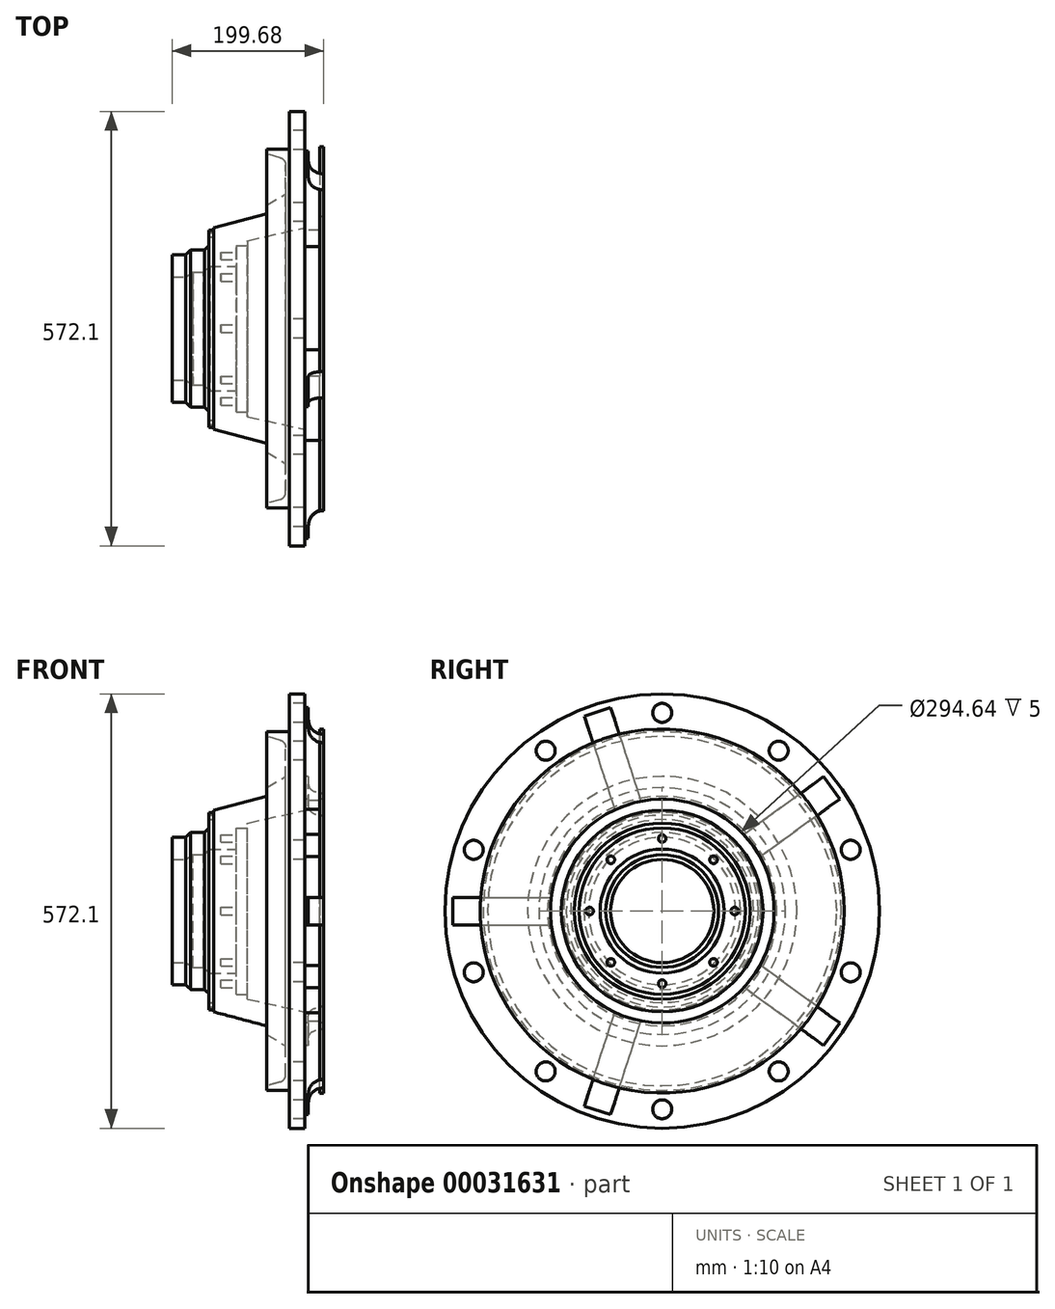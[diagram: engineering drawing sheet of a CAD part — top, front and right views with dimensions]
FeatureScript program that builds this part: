
annotation { "Feature Type Name" : "Feature", "Feature Type Description" : "" }
export const myFeature = defineFeature(function(context is Context, id is Id, definition is map)
    precondition{}
    {
        {
            var Q0;
            Q0=qCreatedBy(makeId("Front.planeOp"),FACE);
            var sketch = newSketch(context, id + "F0", { "sketchPlane" : qUnion([Q0])});
            skLineSegment(sketch, "E0", {"start": v(-16.31, 151.18) * mm, "end": v(-16.31, 189.2) * mm});
            skLineSegment(sketch, "E1", {"start": v(-23.64, 198.84) * mm, "end": v(-41.31, 203.73) * mm});
            skLineSegment(sketch, "E2", {"start": v(-41.31, 203.73) * mm, "end": v(-41.31, 209.73) * mm});
            skLineSegment(sketch, "E3", {"start": v(-41.31, 209.73) * mm, "end": v(-11.31, 209.73) * mm});
            skLineSegment(sketch, "E4", {"start": v(-11.31, 209.73) * mm, "end": v(-11.31, 259.73) * mm});
            skLineSegment(sketch, "E5", {"start": v(-11.31, 259.73) * mm, "end": v(8.69, 259.73) * mm});
            skLineSegment(sketch, "E6", {"start": v(8.69, 106.48) * mm, "end": v(-66.31, 89.52) * mm});
            skLineSegment(sketch, "E7", {"start": v(-66.31, 89.52) * mm, "end": v(-66.31, 83.17) * mm});
            skPoint(sketch, "E8.visualSharp", {"position": v(-16.31, 196.81) * mm});
            skArc(sketch, "E8.filletArc", {"start": v(-16.31, 189.2) * mm, "mid": v(-18.36, 195.26) * mm, "end": v(-23.64, 198.84) * mm});
            skLineSegment(sketch, "E9", {"start": v(-41.31, 124.8) * mm, "end": v(-41.31, 136.18) * mm});
            skLineSegment(sketch, "E10", {"start": v(-41.31, 136.18) * mm, "end": v(-16.31, 151.18) * mm});
            skLineSegment(sketch, "E11", {"start": v(-111.31, 106.4) * mm, "end": v(-41.31, 124.8) * mm});
            skLineSegment(sketch, "E12", {"start": v(-66.31, 83.17) * mm, "end": v(-81.31, 83.17) * mm});
            skLineSegment(sketch, "E13", {"start": v(-81.31, 83.17) * mm, "end": v(-81.31, 55.36) * mm});
            skLineSegment(sketch, "E14", {"start": v(-110.7, 106.4) * mm, "end": v(-111.31, 106.4) * mm});
            skLineSegment(sketch, "E15", {"start": v(-110.7, 106.4) * mm, "end": v(-110.7, 103.57) * mm});
            skLineSegment(sketch, "E16", {"start": v(-110.7, 103.57) * mm, "end": v(-117.24, 103.57) * mm});
            skLineSegment(sketch, "E17", {"start": v(-117.24, 103.57) * mm, "end": v(-117.24, 100.15) * mm});
            skLineSegment(sketch, "E18", {"start": v(-117.24, 100.15) * mm, "end": v(-110.7, 100.15) * mm});
            skLineSegment(sketch, "E19", {"start": v(-110.7, 100.15) * mm, "end": v(-110.7, 94.23) * mm});
            skLineSegment(sketch, "E20", {"start": v(-110.7, 94.23) * mm, "end": v(-117.24, 94.23) * mm});
            skLineSegment(sketch, "E21", {"start": v(-117.24, 94.23) * mm, "end": v(-117.24, 82.72) * mm});
            skLineSegment(sketch, "E22", {"start": v(-117.24, 82.72) * mm, "end": v(-123.31, 76.96) * mm});
            skLineSegment(sketch, "E23", {"start": v(-123.31, 76.96) * mm, "end": v(-141.31, 76.96) * mm});
            skLineSegment(sketch, "E24", {"start": v(-141.31, 76.96) * mm, "end": v(-148, 70.74) * mm});
            skLineSegment(sketch, "E25", {"start": v(-148, 70.74) * mm, "end": v(-166, 70.74) * mm});
            skLineSegment(sketch, "E26", {"start": v(-81.31, 55.36) * mm, "end": v(-116.31, 55.36) * mm});
            skLineSegment(sketch, "E27", {"start": v(-116.31, 55.36) * mm, "end": v(-124.55, 47.96) * mm});
            skLineSegment(sketch, "E28", {"start": v(-124.55, 47.96) * mm, "end": v(-138.27, 47.96) * mm});
            skLineSegment(sketch, "E29", {"start": v(-138.27, 47.96) * mm, "end": v(-147.69, 41.68) * mm});
            skLineSegment(sketch, "E30", {"start": v(-166, 70.74) * mm, "end": v(-166, -26.32) * mm});
            skLineSegment(sketch, "E31", {"start": v(8.69, 259.73) * mm, "end": v(8.69, -26.32) * mm});
            skLineSegment(sketch, "E32", {"start": v(8.69, -26.32) * mm, "end": v(-166, -26.32) * mm, "construction": true});
            skLineSegment(sketch, "E33", {"start": v(-147.69, 41.68) * mm, "end": v(-166, 41.68) * mm});
            skSolve(sketch);
        }
        {
            var Q0;
            Q0=makeQuery(id+"F0.imprint","IMPRINT",FACE,{"disambiguationData":[TD([[makeQuery(id+"F0.imprint","IMPRINT",EDGE,{"derivedFrom":sQuery(id+"F0.wireOp",EDGE,"E0")}),-1.0]])]});
            var Q1;
            Q1=sQuery(id+"F0.wireOp",EDGE,"E32");
            revolve(context, id + "F1", {"entities" : qUnion([Q0]), "axis" : qUnion([Q1]), "revolveType" : RevolveType.FULL});
        }
        {
            var Q0;
            Q0=makeQuery(id+"F1.opRevolve","SWEPT_FACE",FACE,{"disambiguationData":[OSD([sQuery(id+"F0.wireOp",EDGE,"E4")])]});
            var sketch = newSketch(context, id + "F2", { "sketchPlane" : qUnion([Q0])});
            skCircle(sketch, "E34", {"center": v(0, 234.73) * mm, "radius": 12.5 * mm});
            skPoint(sketch, "E35", {"position": v(0, -26.32) * mm});
            skCircle(sketch, "E36.1.0", {"center": v(-153.44, 184.88) * mm, "radius": 12.5 * mm});
            skCircle(sketch, "E36.2.0", {"center": v(-248.27, 54.35) * mm, "radius": 12.5 * mm});
            skCircle(sketch, "E36.3.0", {"center": v(-248.27, -106.99) * mm, "radius": 12.5 * mm});
            skCircle(sketch, "E36.4.0", {"center": v(-153.44, -237.51) * mm, "radius": 12.5 * mm});
            skCircle(sketch, "E36.5.0", {"center": v(0, -287.37) * mm, "radius": 12.5 * mm});
            skCircle(sketch, "E36.6.0", {"center": v(153.44, -237.51) * mm, "radius": 12.5 * mm});
            skCircle(sketch, "E36.7.0", {"center": v(248.27, -106.99) * mm, "radius": 12.5 * mm});
            skCircle(sketch, "E36.8.0", {"center": v(248.27, 54.35) * mm, "radius": 12.5 * mm});
            skCircle(sketch, "E36.9.0", {"center": v(153.44, 184.88) * mm, "radius": 12.5 * mm});
            skSolve(sketch);
        }
        {
            var Q0;
            Q0 = qSketchRegion(id + "F2", true);
            extrude(context, id + "F3", {"entities" : qUnion([Q0]), "operationType" : NewBodyOperationType.REMOVE, "oppositeDirection" : true, "depth" : 20 * mm});
        }
        {
            var Q0;
            Q0=makeQuery(id+"F1.opRevolve","SWEPT_FACE",FACE,{"disambiguationData":[OSD([sQuery(id+"F0.wireOp",EDGE,"E13")])]});
            var sketch = newSketch(context, id + "F4", { "sketchPlane" : qUnion([Q0])});
            skCircle(sketch, "E37", {"center": v(0, 69.27) * mm, "radius": 5 * mm});
            skPoint(sketch, "E38", {"position": v(0, -26.32) * mm});
            skCircle(sketch, "E39.1.0", {"center": v(-67.59, 41.27) * mm, "radius": 5 * mm});
            skCircle(sketch, "E39.2.0", {"center": v(-95.59, -26.32) * mm, "radius": 5 * mm});
            skCircle(sketch, "E39.3.0", {"center": v(-67.59, -93.9) * mm, "radius": 5 * mm});
            skCircle(sketch, "E39.4.0", {"center": v(0, -121.9) * mm, "radius": 5 * mm});
            skCircle(sketch, "E39.5.0", {"center": v(67.59, -93.9) * mm, "radius": 5 * mm});
            skCircle(sketch, "E39.6.0", {"center": v(95.59, -26.32) * mm, "radius": 5 * mm});
            skCircle(sketch, "E39.7.0", {"center": v(67.59, 41.27) * mm, "radius": 5 * mm});
            skSolve(sketch);
        }
        {
            var Q0;
            Q0 = qSketchRegion(id + "F4", true);
            extrude(context, id + "F5", {"entities" : qUnion([Q0]), "operationType" : NewBodyOperationType.REMOVE, "oppositeDirection" : true, "depth" : 20 * mm});
        }
        {
            var Q0;
            Q0=makeQuery(id+"F1.opRevolve","SWEPT_FACE",FACE,{"disambiguationData":[OSD([sQuery(id+"F0.wireOp",EDGE,"E31")])]});
            var sketch = newSketch(context, id + "F6", { "sketchPlane" : qUnion([Q0])});
            skLineSegment(sketch, "E40.bottom", {"start": v(-276.03, -44.49) * mm, "end": v(-147, -44.49) * mm});
            skLineSegment(sketch, "E40.top", {"start": v(-276.03, -8.15) * mm, "end": v(-147, -8.15) * mm});
            skLineSegment(sketch, "E40.left", {"start": v(-276.03, -44.49) * mm, "end": v(-276.03, -8.15) * mm});
            skLineSegment(sketch, "E40.right", {"start": v(-147, -44.49) * mm, "end": v(-147, -8.15) * mm});
            skLineSegment(sketch, "E41.1.0", {"start": v(-68.02, -294.45) * mm, "end": v(-102.58, -283.22) * mm});
            skLineSegment(sketch, "E41.1.1", {"start": v(-68.02, -294.45) * mm, "end": v(-28.15, -171.74) * mm});
            skLineSegment(sketch, "E41.1.2", {"start": v(-102.58, -283.22) * mm, "end": v(-62.7, -160.51) * mm});
            skLineSegment(sketch, "E41.1.3", {"start": v(-28.15, -171.74) * mm, "end": v(-62.7, -160.51) * mm});
            skLineSegment(sketch, "E41.2.0", {"start": v(234, -173.86) * mm, "end": v(212.63, -203.26) * mm});
            skLineSegment(sketch, "E41.2.1", {"start": v(234, -173.86) * mm, "end": v(129.6, -98.02) * mm});
            skLineSegment(sketch, "E41.2.2", {"start": v(212.63, -203.26) * mm, "end": v(108.25, -127.42) * mm});
            skLineSegment(sketch, "E41.2.3", {"start": v(129.6, -98.02) * mm, "end": v(108.25, -127.42) * mm});
            skLineSegment(sketch, "E41.3.0", {"start": v(212.63, 150.63) * mm, "end": v(234, 121.23) * mm});
            skLineSegment(sketch, "E41.3.1", {"start": v(212.63, 150.63) * mm, "end": v(108.25, 74.79) * mm});
            skLineSegment(sketch, "E41.3.2", {"start": v(234, 121.23) * mm, "end": v(129.6, 45.4) * mm});
            skLineSegment(sketch, "E41.3.3", {"start": v(108.25, 74.79) * mm, "end": v(129.6, 45.4) * mm});
            skLineSegment(sketch, "E41.4.0", {"start": v(-102.58, 230.59) * mm, "end": v(-68.02, 241.82) * mm});
            skLineSegment(sketch, "E41.4.1", {"start": v(-102.58, 230.59) * mm, "end": v(-62.7, 107.88) * mm});
            skLineSegment(sketch, "E41.4.2", {"start": v(-68.02, 241.82) * mm, "end": v(-28.15, 119.1) * mm});
            skLineSegment(sketch, "E41.4.3", {"start": v(-62.7, 107.88) * mm, "end": v(-28.15, 119.1) * mm});
            skPoint(sketch, "E41.center", {"position": v(0, -26.32) * mm});
            skSolve(sketch);
        }
        {
            var Q0;
            Q0 = qSketchRegion(id + "F6", true);
            extrude(context, id + "F7", {"entities" : qUnion([Q0]), "operationType" : NewBodyOperationType.ADD, "depth" : 20 * mm});
        }
        {
            var Q0;
            Q0=makeQuery(id+"F7.opExtrude","CAP_FACE",FACE,{"disambiguationData":[OSD([sQuery(id+"F6.wireOp",EDGE,"E40.bottom"),sQuery(id+"F6.wireOp",EDGE,"E40.top"),sQuery(id+"F6.wireOp",EDGE,"E40.left"),sQuery(id+"F6.wireOp",EDGE,"E40.right")])],"isStart":false});
            var sketch = newSketch(context, id + "F8", { "sketchPlane" : qUnion([Q0])});
            skCircle(sketch, "E42", {"center": v(0, -26.32) * mm, "radius": 239.7 * mm});
            skPoint(sketch, "E42.centerSnap0", {"position": v(-276.03, -26.32) * mm});
            skCircle(sketch, "E43", {"center": v(0, -26.32) * mm, "radius": 147.32 * mm});
            skSolve(sketch);
        }
        {
            var Q0;
            {var subQ1=makeQuery(id+"F7.opExtrude","CAP_EDGE",EDGE,{"disambiguationData":[OSD([sQuery(id+"F6.wireOp",EDGE,"E40.bottom")])],"isStart":false});var subQ3=sQuery(id+"F8.wireOp",EDGE,"E42");var subQ4=makeQuery(id+"F8.imprint","INTERSECT",VERTEX,{"derivedFrom":[subQ1,subQ3]});Q0=makeQuery(id+"F8.imprint","IMPRINT",FACE,{"disambiguationData":[TD([[makeQuery(id+"F8.imprint","IMPRINT",EDGE,{"disambiguationData":[TD([[subQ4,1.0]])],"derivedFrom":subQ3}),1.0]])]});}
            var Q1;
            {var subQ1=makeQuery(id+"F7.opExtrude","CAP_EDGE",EDGE,{"disambiguationData":[OSD([sQuery(id+"F6.wireOp",EDGE,"E40.bottom")])],"isStart":false});var subQ3=sQuery(id+"F8.wireOp",EDGE,"E42");var subQ4=makeQuery(id+"F8.imprint","INTERSECT",VERTEX,{"derivedFrom":[subQ1,subQ3]});Q1=makeQuery(id+"F8.imprint","IMPRINT",FACE,{"disambiguationData":[TD([[makeQuery(id+"F8.imprint","IMPRINT",EDGE,{"disambiguationData":[TD([[subQ4,-1.0]])],"derivedFrom":subQ3}),1.0]])]});}
            extrude(context, id + "F9", {"entities" : qUnion([Q0, Q1]), "operationType" : NewBodyOperationType.ADD, "depth" : 5 * mm});
        }
        {
            var Q0;
            {var subQ0=sQuery(id+"F6.wireOp",EDGE,"E41.1.2");var subQ2=sQuery(id+"F6.wireOp",EDGE,"E41.1.1");var subQ3=sQuery(id+"F6.wireOp",EDGE,"E41.1.0");Q0=makeQuery(id+"F9.boolean.opBoolean","SPLIT",FACE,{"disambiguationData":[TD([makeQuery(id+"F7.opExtrude","SWEPT_FACE",FACE,{"disambiguationData":[OSD([subQ3])]})])],"derivedFrom":makeQuery(id+"F7.opExtrude","CAP_FACE",FACE,{"disambiguationData":[OSD([subQ3,subQ2,subQ0,sQuery(id+"F6.wireOp",EDGE,"E41.1.3")])],"isStart":false})});}
            var Q1;
            {var subQ1=sQuery(id+"F6.wireOp",EDGE,"E40.left");var subQ2=sQuery(id+"F6.wireOp",EDGE,"E40.top");var subQ3=sQuery(id+"F6.wireOp",EDGE,"E40.bottom");Q1=makeQuery(id+"F9.boolean.opBoolean","SPLIT",FACE,{"disambiguationData":[TD([makeQuery(id+"F7.opExtrude","SWEPT_FACE",FACE,{"disambiguationData":[OSD([subQ3])]})])],"derivedFrom":makeQuery(id+"F7.opExtrude","CAP_FACE",FACE,{"disambiguationData":[OSD([subQ3,subQ2,subQ1,sQuery(id+"F6.wireOp",EDGE,"E40.right")])],"isStart":false})});}
            var Q2;
            {var subQ1=sQuery(id+"F6.wireOp",EDGE,"E41.2.2");var subQ2=sQuery(id+"F6.wireOp",EDGE,"E41.2.1");var subQ3=sQuery(id+"F6.wireOp",EDGE,"E41.2.0");Q2=makeQuery(id+"F9.boolean.opBoolean","SPLIT",FACE,{"disambiguationData":[TD([makeQuery(id+"F7.opExtrude","SWEPT_FACE",FACE,{"disambiguationData":[OSD([subQ3])]})])],"derivedFrom":makeQuery(id+"F7.opExtrude","CAP_FACE",FACE,{"disambiguationData":[OSD([subQ3,subQ2,subQ1,sQuery(id+"F6.wireOp",EDGE,"E41.2.3")])],"isStart":false})});}
            var Q3;
            {var subQ0=sQuery(id+"F6.wireOp",EDGE,"E41.4.2");var subQ2=sQuery(id+"F6.wireOp",EDGE,"E41.4.1");var subQ3=sQuery(id+"F6.wireOp",EDGE,"E41.4.0");Q3=makeQuery(id+"F9.boolean.opBoolean","SPLIT",FACE,{"disambiguationData":[TD([makeQuery(id+"F7.opExtrude","SWEPT_FACE",FACE,{"disambiguationData":[OSD([subQ3])]})])],"derivedFrom":makeQuery(id+"F7.opExtrude","CAP_FACE",FACE,{"disambiguationData":[OSD([subQ3,subQ2,subQ0,sQuery(id+"F6.wireOp",EDGE,"E41.4.3")])],"isStart":false})});}
            var Q4;
            {var subQ1=sQuery(id+"F6.wireOp",EDGE,"E41.3.2");var subQ2=sQuery(id+"F6.wireOp",EDGE,"E41.3.1");var subQ3=sQuery(id+"F6.wireOp",EDGE,"E41.3.0");Q4=makeQuery(id+"F9.boolean.opBoolean","SPLIT",FACE,{"disambiguationData":[TD([makeQuery(id+"F7.opExtrude","SWEPT_FACE",FACE,{"disambiguationData":[OSD([subQ3])]})])],"derivedFrom":makeQuery(id+"F7.opExtrude","CAP_FACE",FACE,{"disambiguationData":[OSD([subQ3,subQ2,subQ1,sQuery(id+"F6.wireOp",EDGE,"E41.3.3")])],"isStart":false})});}
            extrude(context, id + "F10", {"entities" : qUnion([Q0, Q1, Q2, Q3, Q4]), "operationType" : NewBodyOperationType.REMOVE, "oppositeDirection" : true, "depth" : 15 * mm});
        }
        {
            var Q0;
            {var subQ0=sQuery(id+"F8.wireOp",EDGE,"E42");Q0=makeQuery(id+"F10.boolean.opBoolean","COPY",EDGE,{"derivedFrom":makeQuery(id+"F10.opExtrude","CAP_EDGE",EDGE,{"disambiguationData":[OSD([subQ0]),TDD([makeQuery(id+"F9.boolean.opBoolean","SPLIT",EDGE,{"disambiguationData":[topologyDisambiguationEdgeConnected([makeQuery(id+"F7.opExtrude","CAP_FACE",FACE,{"disambiguationData":[OSD([sQuery(id+"F6.wireOp",EDGE,"E41.2.0"),sQuery(id+"F6.wireOp",EDGE,"E41.2.1"),sQuery(id+"F6.wireOp",EDGE,"E41.2.2"),sQuery(id+"F6.wireOp",EDGE,"E41.2.3")])],"isStart":false}),makeQuery(id+"F9.opExtrude","SWEPT_FACE",FACE,{"disambiguationData":[OSD([subQ0])]})])],"derivedFrom":makeQuery(id+"F9.opExtrude","CAP_EDGE",EDGE,{"disambiguationData":[OSD([subQ0])],"isStart":true})})])],"isStart":false})});}
            var Q1;
            {var subQ0=sQuery(id+"F8.wireOp",EDGE,"E42");Q1=makeQuery(id+"F10.boolean.opBoolean","COPY",EDGE,{"derivedFrom":makeQuery(id+"F10.opExtrude","CAP_EDGE",EDGE,{"disambiguationData":[OSD([subQ0]),TDD([makeQuery(id+"F9.boolean.opBoolean","SPLIT",EDGE,{"disambiguationData":[topologyDisambiguationEdgeConnected([makeQuery(id+"F7.opExtrude","CAP_FACE",FACE,{"disambiguationData":[OSD([sQuery(id+"F6.wireOp",EDGE,"E41.3.0"),sQuery(id+"F6.wireOp",EDGE,"E41.3.1"),sQuery(id+"F6.wireOp",EDGE,"E41.3.2"),sQuery(id+"F6.wireOp",EDGE,"E41.3.3")])],"isStart":false}),makeQuery(id+"F9.opExtrude","SWEPT_FACE",FACE,{"disambiguationData":[OSD([subQ0])]})])],"derivedFrom":makeQuery(id+"F9.opExtrude","CAP_EDGE",EDGE,{"disambiguationData":[OSD([subQ0])],"isStart":true})})])],"isStart":false})});}
            var Q2;
            {var subQ0=sQuery(id+"F8.wireOp",EDGE,"E42");Q2=makeQuery(id+"F10.boolean.opBoolean","COPY",EDGE,{"derivedFrom":makeQuery(id+"F10.opExtrude","CAP_EDGE",EDGE,{"disambiguationData":[OSD([subQ0]),TDD([makeQuery(id+"F9.boolean.opBoolean","SPLIT",EDGE,{"disambiguationData":[topologyDisambiguationEdgeConnected([makeQuery(id+"F7.opExtrude","CAP_FACE",FACE,{"disambiguationData":[OSD([sQuery(id+"F6.wireOp",EDGE,"E41.4.0"),sQuery(id+"F6.wireOp",EDGE,"E41.4.1"),sQuery(id+"F6.wireOp",EDGE,"E41.4.2"),sQuery(id+"F6.wireOp",EDGE,"E41.4.3")])],"isStart":false}),makeQuery(id+"F9.opExtrude","SWEPT_FACE",FACE,{"disambiguationData":[OSD([subQ0])]})])],"derivedFrom":makeQuery(id+"F9.opExtrude","CAP_EDGE",EDGE,{"disambiguationData":[OSD([subQ0])],"isStart":true})})])],"isStart":false})});}
            var Q3;
            {var subQ0=sQuery(id+"F8.wireOp",EDGE,"E42");Q3=makeQuery(id+"F10.boolean.opBoolean","COPY",EDGE,{"derivedFrom":makeQuery(id+"F10.opExtrude","CAP_EDGE",EDGE,{"disambiguationData":[OSD([subQ0]),TDD([makeQuery(id+"F9.boolean.opBoolean","SPLIT",EDGE,{"disambiguationData":[topologyDisambiguationEdgeConnected([makeQuery(id+"F7.opExtrude","CAP_FACE",FACE,{"disambiguationData":[OSD([sQuery(id+"F6.wireOp",EDGE,"E40.bottom"),sQuery(id+"F6.wireOp",EDGE,"E40.top"),sQuery(id+"F6.wireOp",EDGE,"E40.left"),sQuery(id+"F6.wireOp",EDGE,"E40.right")])],"isStart":false}),makeQuery(id+"F9.opExtrude","SWEPT_FACE",FACE,{"disambiguationData":[OSD([subQ0])]})])],"derivedFrom":makeQuery(id+"F9.opExtrude","CAP_EDGE",EDGE,{"disambiguationData":[OSD([subQ0])],"isStart":true})})])],"isStart":false})});}
            var Q4;
            {var subQ0=sQuery(id+"F8.wireOp",EDGE,"E42");Q4=makeQuery(id+"F10.boolean.opBoolean","COPY",EDGE,{"derivedFrom":makeQuery(id+"F10.opExtrude","CAP_EDGE",EDGE,{"disambiguationData":[OSD([subQ0]),TDD([makeQuery(id+"F9.boolean.opBoolean","SPLIT",EDGE,{"disambiguationData":[topologyDisambiguationEdgeConnected([makeQuery(id+"F7.opExtrude","CAP_FACE",FACE,{"disambiguationData":[OSD([sQuery(id+"F6.wireOp",EDGE,"E41.1.0"),sQuery(id+"F6.wireOp",EDGE,"E41.1.1"),sQuery(id+"F6.wireOp",EDGE,"E41.1.2"),sQuery(id+"F6.wireOp",EDGE,"E41.1.3")])],"isStart":false}),makeQuery(id+"F9.opExtrude","SWEPT_FACE",FACE,{"disambiguationData":[OSD([subQ0])]})])],"derivedFrom":makeQuery(id+"F9.opExtrude","CAP_EDGE",EDGE,{"disambiguationData":[OSD([subQ0])],"isStart":true})})])],"isStart":false})});}
            fillet(context, id + "F11", {"entities" : qUnion([Q0, Q1, Q2, Q3, Q4]), "radius" : 20 * mm, "tangentPropagation" : true, "allowEdgeOverflow" : false});
        }
    });
